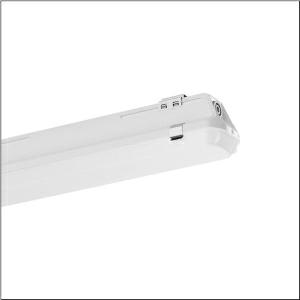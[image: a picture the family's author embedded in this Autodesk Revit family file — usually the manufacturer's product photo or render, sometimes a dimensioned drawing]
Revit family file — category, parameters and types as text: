
# Revit family: monsun_r__11_emergency_51fp107p467h3g_a613
name_source: partatom
category: Lighting Fixtures
units: mm (PartAtom-declared; Revit-internal decimal feet)

## family parameters
Cut with Voids When Loaded = No
Host = Face
Light Source = No
Part Type = Normal
Room Calculation Point = No
Round Connector Dimension = Use Diameter
Shared = No

## types (1)
- Monsun® 11 emergency (1 x LED, 6050 lm, 37.2 W, 4000K)
    Apparent Load = 37 VA
    CIE Flux Codes = 47 77 93 94 100
    Color Rendering = 80
    Color Temperature = 4000K
    Default Elevation = 1800 mm
    Description = Monsun® 11 emergency, damp-proof luminaire, chain hanger, primary optical cover: enclosure, of PMMA, light emission: direct distribution, primary light characteristic: symmetric, installation type: suspended mounting, surface-mounted, horizontal mounting, vertical mounting, LED, rated luminous flux: 6.050lm, luminous efficacy: 163lm/W, light colour: 840, colour temperature: 4000K, control gear: ECG, with terminal, 4-pole, max. 2.5mm², mains connection: 220..240V, AC, 50/60Hz, rated input power: 37W, control gear: single battery element, battery: NiCd, 4,5Ah, mains connection: 230V, 50Hz, luminaire housing, of glass-fibre reinforced polyester, uncoated, bright grey, incl. chain hanger, length: 1.590mm, width: 90mm, height: 88mm, clip for enclosure, of stainless steel (V2A), ceiling mounting element, of stainless steel (V2A), chain hanger, of stainless steel (V2A), protection rating (complete): IP66, insulation class (complete): insulation class I (protective earthing), certification: CE, UKCA, protection symbol: D, impact resistance: IK04, permissible operating ambient temperature: +5..+35°C, standard: EN 50419, EN 60598-2-1, EN 60598-2-22, no direct snow, no direct sun, no direct rain, for indoor or canopied outdoor use, corresponds to IFS (International Featured Standards) requirements for safety and quality in the food industry, contact your sales advisor before using the luminaires in applications with unclear chemical exposure, large temperature fluctuations or condensation-forming humidity, LABS conformity tested according to VDMA 24364:2018-05, packaging unit: 1 piece
    Height = 89 mm
    Lamp = 1 x LED
    Lamp Light Flux = 6050 lm
    Lamp Power = 37.2 W
    Lamp count = 1
    Length = 1590 mm
    Luminous efficacy = 163 lm/W
    Manufacturer = Siteco
    ModVariant = No
    Model = 51FP107P467H3G
    Mounting Place = Ceiling
    Mounting Type = Surface mounted
    Number of Poles = 1
    OnlyDefault = Yes
    Power Factor = 1
    Product Name = Monsun® 11 emergency
    Product group = damp-proof luminaire
    ProductGroupID = 300
    Protection Class = Protection class I
    Protection Degree = IP 66
    RLX_Detail_Level = 1
    RLX_Emergency_Light_Flux = 0 lm
    RLX_Emergency_Type = 0
    RLX_Emergency_Type_DB = No
    RlxData = <blob elided: 88885 chars, md5=1a02b169>
    Socket = socket
    Standby Power = 0 W
    System Light Flux = 6050 lm
    System Power = 37 W
    Type Comments = Product without accessories
    Type Image = l_1004748.jpg
    URL = http://relux.com
    VarID = ---
    Voltage = 0 V
    Weight = 0.00 kg
    Width = 90 mm

## geometry (parser evidence)
native form markers: Blend x4, Sweep x13
no freeform markers — native parametric forms only
